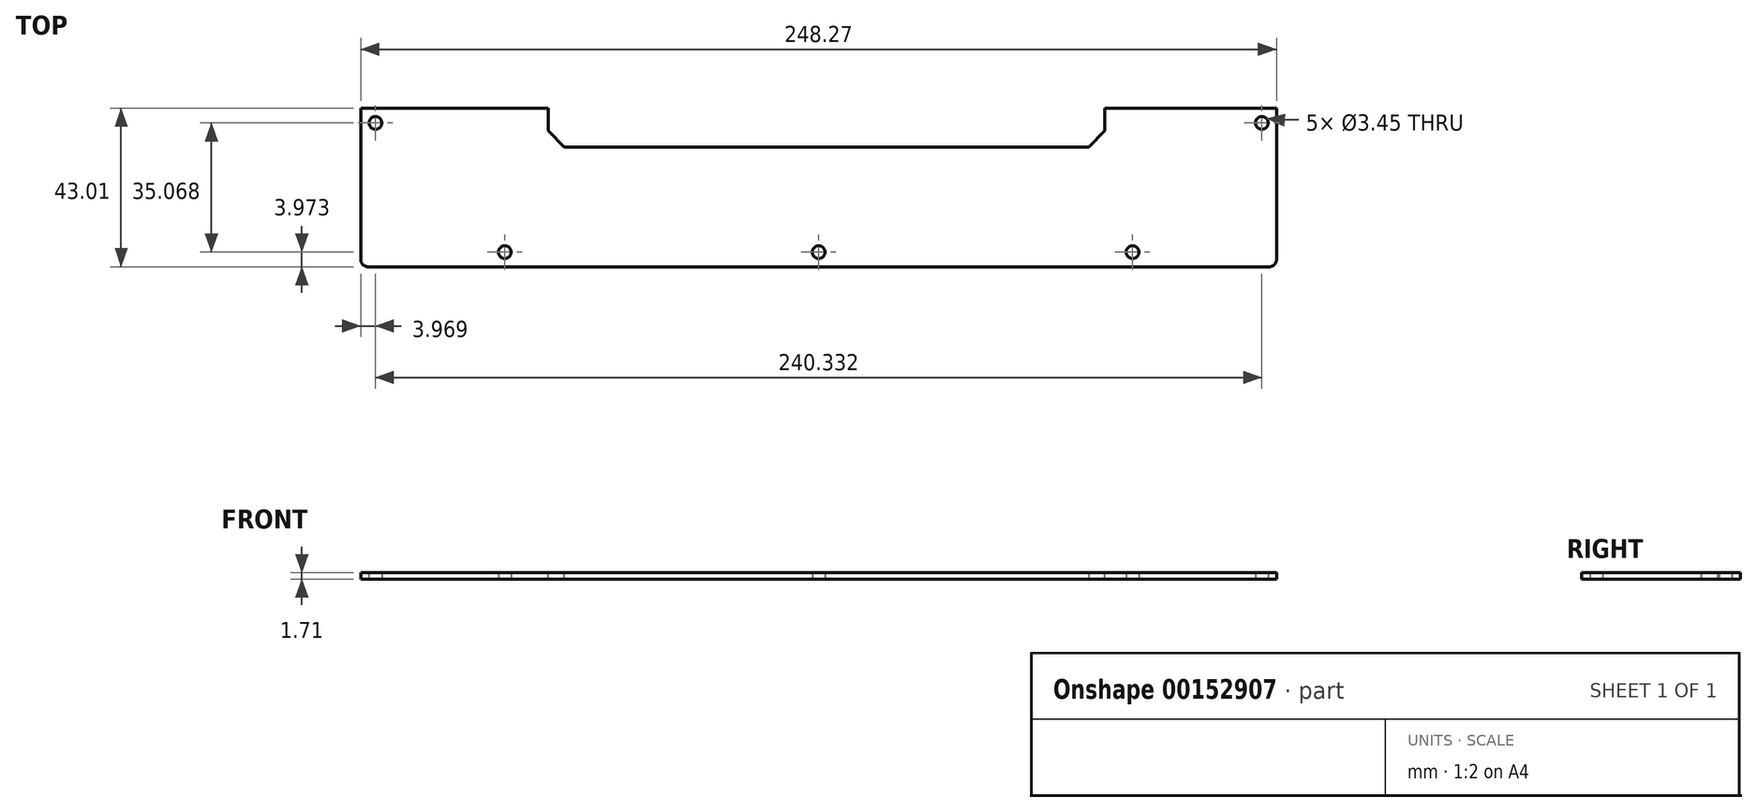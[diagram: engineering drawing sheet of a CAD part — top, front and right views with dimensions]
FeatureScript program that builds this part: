
annotation { "Feature Type Name" : "Feature", "Feature Type Description" : "" }
export const myFeature = defineFeature(function(context is Context, id is Id, definition is map)
    precondition{}
    {
        {
            var Q0;
            Q0=qCreatedBy(makeId("Top.planeOp"),FACE);
            var sketch = newSketch(context, id + "F0", { "sketchPlane" : qUnion([Q0])});
            skLineSegment(sketch, "E0.bottom", {"start": v(0, 0) * mm, "end": v(248.27, 0) * mm});
            skLineSegment(sketch, "E0.top", {"start": v(0, -43) * mm, "end": v(248.27, -43) * mm});
            skLineSegment(sketch, "E0.left", {"start": v(0, 0) * mm, "end": v(0, -43) * mm});
            skLineSegment(sketch, "E0.right", {"start": v(248.27, 0) * mm, "end": v(248.27, -43) * mm});
            skLineSegment(sketch, "E1", {"start": v(0, -3.97) * mm, "end": v(3.97, -3.97) * mm, "construction": true});
            skLineSegment(sketch, "E2", {"start": v(3.97, -3.97) * mm, "end": v(3.97, 0) * mm, "construction": true});
            skLineSegment(sketch, "E3", {"start": v(244.3, 0) * mm, "end": v(244.3, -3.97) * mm, "construction": true});
            skLineSegment(sketch, "E4", {"start": v(244.3, -3.97) * mm, "end": v(248.27, -3.97) * mm, "construction": true});
            skLineSegment(sketch, "E5", {"start": v(124.13, -43) * mm, "end": v(124.13, -39.04) * mm, "construction": true});
            skLineSegment(sketch, "E6", {"start": v(124.13, -39.04) * mm, "end": v(209.23, -39.04) * mm, "construction": true});
            skLineSegment(sketch, "E7", {"start": v(124.13, -39.04) * mm, "end": v(39.04, -39.04) * mm, "construction": true});
            skCircle(sketch, "E8", {"center": v(3.97, -3.97) * mm, "radius": 1.73 * mm});
            skCircle(sketch, "E9", {"center": v(39.04, -39.04) * mm, "radius": 1.73 * mm});
            skCircle(sketch, "E10", {"center": v(124.13, -39.04) * mm, "radius": 1.73 * mm});
            skCircle(sketch, "E11", {"center": v(209.23, -39.04) * mm, "radius": 1.73 * mm});
            skCircle(sketch, "E12", {"center": v(244.3, -3.97) * mm, "radius": 1.73 * mm});
            skLineSegment(sketch, "E13", {"start": v(209.23, -39.04) * mm, "end": v(209.23, -3.97) * mm, "construction": true});
            skLineSegment(sketch, "E14", {"start": v(209.23, -3.97) * mm, "end": v(244.3, -3.97) * mm, "construction": true});
            skSolve(sketch);
        }
        {
            var Q0;
            Q0=qSketchRegion(id+"F0",true);
            extrude(context, id + "F1", {"entities" : qUnion([Q0]), "depth" : 1.7 * mm});
        }
        {
            var Q0;
            Q0=makeQuery(id+"F1.opExtrude","SWEPT_EDGE",EDGE,{"disambiguationData":[OSD([sQuery(id+"F0.wireOp",EDGE,"E0.top"),sQuery(id+"F0.wireOp",EDGE,"E0.left")])]});
            var Q1;
            Q1=makeQuery(id+"F1.opExtrude","SWEPT_EDGE",EDGE,{"disambiguationData":[OSD([sQuery(id+"F0.wireOp",EDGE,"E0.top"),sQuery(id+"F0.wireOp",EDGE,"E0.right")])]});
            fillet(context, id + "F2", {"entities" : qUnion([Q0, Q1]), "radius" : 1.98 * mm, "tangentPropagation" : true, "allowEdgeOverflow" : false});
        }
        {
            var Q0;
            Q0=makeQuery(id+"F1.opExtrude","CAP_FACE",FACE,{"disambiguationData":[OSD([sQuery(id+"F0.wireOp",EDGE,"E0.bottom"),sQuery(id+"F0.wireOp",EDGE,"E0.top"),sQuery(id+"F0.wireOp",EDGE,"E0.left"),sQuery(id+"F0.wireOp",EDGE,"E0.right"),sQuery(id+"F0.wireOp",EDGE,"E8"),sQuery(id+"F0.wireOp",EDGE,"E9"),sQuery(id+"F0.wireOp",EDGE,"E10"),sQuery(id+"F0.wireOp",EDGE,"E11"),sQuery(id+"F0.wireOp",EDGE,"E12")])],"isStart":false});
            var sketch = newSketch(context, id + "F3", { "sketchPlane" : qUnion([Q0])});
            skLineSegment(sketch, "E15.bottom", {"start": v(50.78, 0) * mm, "end": v(201.74, 0) * mm});
            skLineSegment(sketch, "E15.top", {"start": v(50.78, -10.47) * mm, "end": v(201.74, -10.47) * mm});
            skLineSegment(sketch, "E15.left", {"start": v(50.78, 0) * mm, "end": v(50.78, -10.47) * mm});
            skLineSegment(sketch, "E15.right", {"start": v(201.74, 0) * mm, "end": v(201.74, -10.47) * mm});
            skLineSegment(sketch, "E16", {"start": v(3.97, -3.97) * mm, "end": v(50.78, -3.97) * mm, "construction": true});
            skSolve(sketch);
        }
        {
            var Q0;
            Q0 = qSketchRegion(id + "F3", true);
            var Q1;
            Q1=makeQuery(id+"F1.opExtrude","CAP_FACE",FACE,{"disambiguationData":[OSD([sQuery(id+"F0.wireOp",EDGE,"E0.bottom"),sQuery(id+"F0.wireOp",EDGE,"E0.top"),sQuery(id+"F0.wireOp",EDGE,"E0.left"),sQuery(id+"F0.wireOp",EDGE,"E0.right"),sQuery(id+"F0.wireOp",EDGE,"E8"),sQuery(id+"F0.wireOp",EDGE,"E9"),sQuery(id+"F0.wireOp",EDGE,"E10"),sQuery(id+"F0.wireOp",EDGE,"E11"),sQuery(id+"F0.wireOp",EDGE,"E12")])],"isStart":true});
            extrude(context, id + "F4", {"entities" : qUnion([Q0]), "operationType" : NewBodyOperationType.REMOVE, "endBound" : BoundingType.UP_TO_SURFACE, "oppositeDirection" : true, "endBoundEntityFace" : qUnion([Q1]), "depth" : 25.4 * mm});
        }
        {
            var Q0;
            Q0=makeQuery(id+"F4.boolean.opBoolean","COPY",EDGE,{"derivedFrom":makeQuery(id+"F4.opExtrude","SWEPT_EDGE",EDGE,{"disambiguationData":[OSD([sQuery(id+"F3.wireOp",EDGE,"E15.top"),sQuery(id+"F3.wireOp",EDGE,"E15.left")])]})});
            var Q1;
            Q1=makeQuery(id+"F4.boolean.opBoolean","COPY",EDGE,{"derivedFrom":makeQuery(id+"F4.opExtrude","SWEPT_EDGE",EDGE,{"disambiguationData":[OSD([sQuery(id+"F3.wireOp",EDGE,"E15.top"),sQuery(id+"F3.wireOp",EDGE,"E15.right")])]})});
            chamfer(context, id + "F5", {"entities" : qUnion([Q0, Q1]), "width" : 4.42 * mm, "tangentPropagation" : true});
        }
    });
